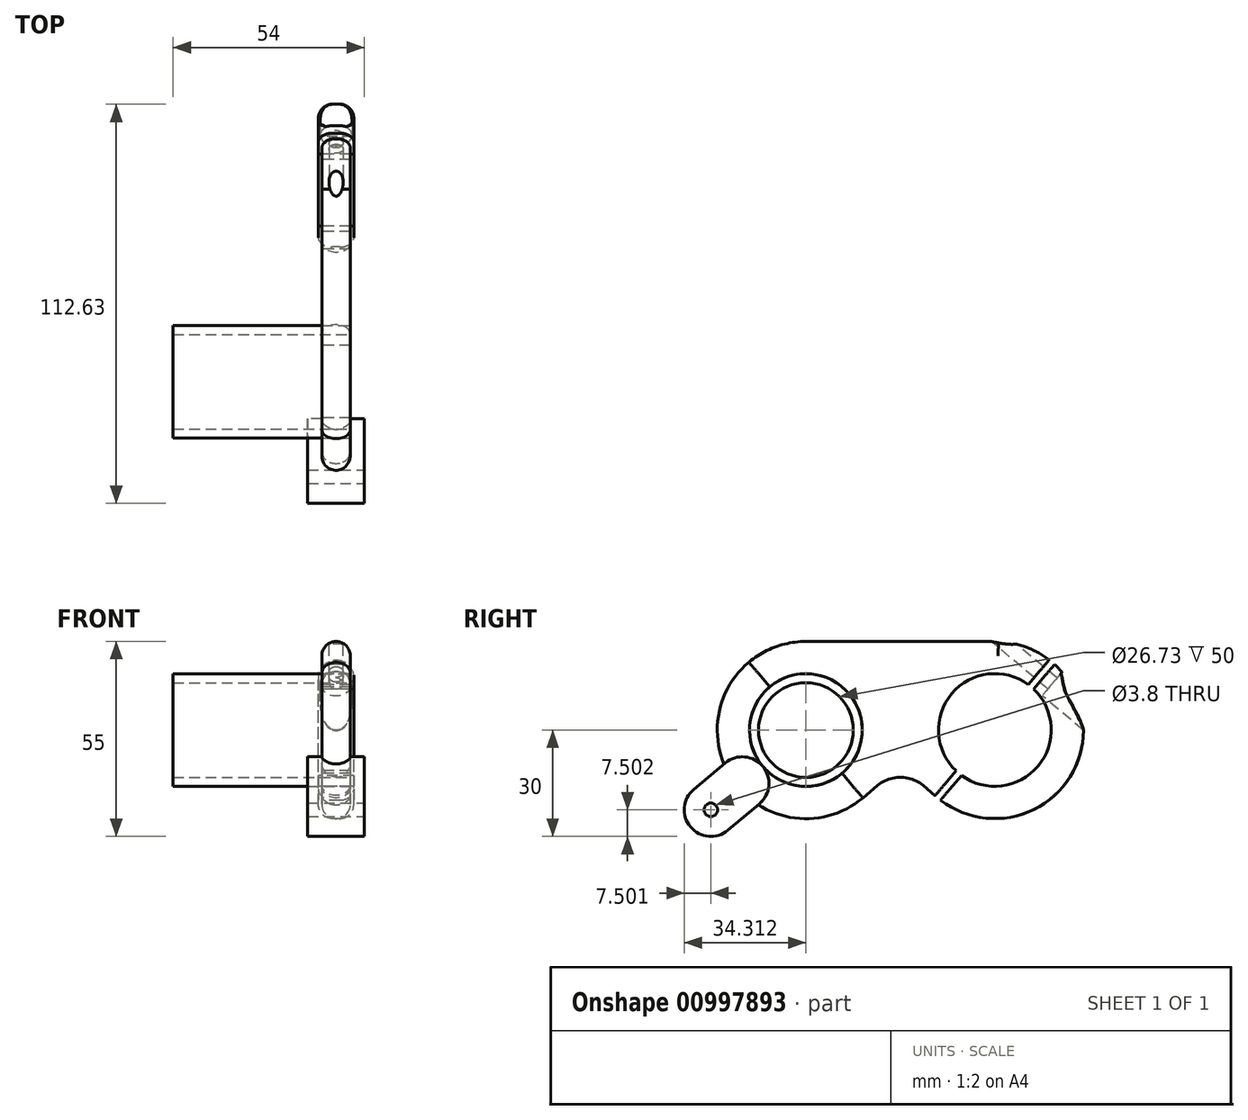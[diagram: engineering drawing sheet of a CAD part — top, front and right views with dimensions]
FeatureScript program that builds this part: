
annotation { "Feature Type Name" : "Feature", "Feature Type Description" : "" }
export const myFeature = defineFeature(function(context is Context, id is Id, definition is map)
    precondition{}
    {
        {
            var Q0;
            Q0=qCreatedBy(makeId("Right.planeOp"),FACE);
            var sketch = newSketch(context, id + "F0", { "sketchPlane" : qUnion([Q0])});
            skCircle(sketch, "E0", {"center": v(0, 0) * mm, "radius": 15.9 * mm});
            skLineSegment(sketch, "E1", {"start": v(-70.5, -0.02) * mm, "end": v(-53.32, -0.02) * mm, "construction": true});
            skCircle(sketch, "E2", {"center": v(-53.32, -0.02) * mm, "radius": 25 * mm});
            skLineSegment(sketch, "E3", {"start": v(-53.32, -0.02) * mm, "end": v(-53.32, 24.98) * mm, "construction": true});
            skLineSegment(sketch, "E4", {"start": v(-53.32, -0.02) * mm, "end": v(-53.32, -25.02) * mm, "construction": true});
            skCircle(sketch, "E5", {"center": v(-80.13, -22.52) * mm, "radius": 7.5 * mm});
            skLineSegment(sketch, "E6", {"start": v(-53.32, -0.02) * mm, "end": v(-80.13, -22.52) * mm, "construction": true});
            skCircle(sketch, "E7", {"center": v(-80.13, -22.52) * mm, "radius": 1.9 * mm});
            skLineSegment(sketch, "E8", {"start": v(-80.13, -22.52) * mm, "end": v(-75.3, -28.26) * mm, "construction": true});
            skLineSegment(sketch, "E9", {"start": v(-80.13, -22.52) * mm, "end": v(-84.95, -16.77) * mm, "construction": true});
            skCircle(sketch, "E10", {"center": v(-53.32, -0.02) * mm, "radius": 15.9 * mm});
            skLineSegment(sketch, "E11", {"start": v(0, 0) * mm, "end": v(0, 15.9) * mm, "construction": true});
            skLineSegment(sketch, "E12", {"start": v(0, 0) * mm, "end": v(0, -15.9) * mm, "construction": true});
            skLineSegment(sketch, "E13", {"start": v(1, 15.87) * mm, "end": v(1, 24.98) * mm});
            skCircle(sketch, "E14.converted", {"center": v(0, 0) * mm, "radius": 25 * mm});
            skLineSegment(sketch, "E15", {"start": v(1, 24.98) * mm, "end": v(-53.32, 24.98) * mm});
            skLineSegment(sketch, "E16", {"start": v(-53.32, -0.02) * mm, "end": v(-69.39, 19.13) * mm});
            skLineSegment(sketch, "E17", {"start": v(-53.32, -0.02) * mm, "end": v(-37.25, -19.17) * mm});
            skLineSegment(sketch, "E18", {"start": v(-37.25, -19.17) * mm, "end": v(-26.65, -10.28) * mm});
            skLineSegment(sketch, "E19", {"start": v(16.07, 19.15) * mm, "end": v(-16.07, -19.15) * mm, "construction": true});
            skLineSegment(sketch, "E20", {"start": v(-16.07, -19.15) * mm, "end": v(-26.65, -10.28) * mm});
            skLineSegment(sketch, "E21", {"start": v(16.82, 18.5) * mm, "end": v(-15.3, -19.78) * mm});
            skLineSegment(sketch, "E22", {"start": v(19.58, 15.55) * mm, "end": v(14.95, 10.03) * mm});
            skLineSegment(sketch, "E23", {"start": v(14.95, 10.03) * mm, "end": v(24.95, 1.65) * mm});
            skLineSegment(sketch, "E24", {"start": v(15.3, 19.78) * mm, "end": v(-16.84, -18.5) * mm});
            skLineSegment(sketch, "E25", {"start": v(-11.91, -21.98) * mm, "end": v(-7.51, -16.73) * mm});
            skLineSegment(sketch, "E26", {"start": v(-7.51, -16.73) * mm, "end": v(2.23, -24.9) * mm});
            skPoint(sketch, "E27", {"position": v(13.18, 15.7) * mm});
            skLineSegment(sketch, "E28", {"start": v(13.18, 15.7) * mm, "end": v(10.9, 17.62) * mm, "construction": true});
            skLineSegment(sketch, "E29", {"start": v(-84.95, -16.77) * mm, "end": v(-73.88, -7.48) * mm});
            skLineSegment(sketch, "E30", {"start": v(-75.3, -28.26) * mm, "end": v(-64.24, -18.97) * mm});
            skLineSegment(sketch, "E31", {"start": v(-73.88, -7.48) * mm, "end": v(-68.88, -3.29) * mm});
            skLineSegment(sketch, "E32", {"start": v(-59.38, -14.72) * mm, "end": v(-64.24, -18.97) * mm});
            skSolve(sketch);
        }
        {
            var Q0;
            {var subQ4=sQuery(id+"F0.wireOp",EDGE,"4b9Ultii-NDLb-Hdy1-wgni-m4wKdF3KNtY6");Q0=makeQuery(id+"F0.imprint","IMPRINT",FACE,{"disambiguationData":[TD([[makeQuery(id+"F0.imprint","IMPRINT",EDGE,{"derivedFrom":subQ4}),1.0]])]});}
            var Q1;
            {var subQ6=sQuery(id+"F0.wireOp",EDGE,"Wf0zkuJS-PnXJ-hlOs-DL1g-wqgcpQEXs6ay");var subQ7=sQuery(id+"F0.wireOp",EDGE,"r5HR3Vc3-aV66-gJRk-fCIw-dcTSZV9Szoix");var subQ8=makeQuery(id+"F0.imprint","INTERSECT",VERTEX,{"derivedFrom":[subQ7,subQ6]});Q1=makeQuery(id+"F0.imprint","IMPRINT",FACE,{"disambiguationData":[TD([[makeQuery(id+"F0.imprint","IMPRINT",EDGE,{"disambiguationData":[TD([[subQ8,1.0]])],"derivedFrom":subQ7}),-1.0]])]});}
            var Q2;
            {var subQ4=sQuery(id+"F0.wireOp",EDGE,"J3v9ANAV-t0TG-syF7-68v8-S9FZO05cP5r5");Q2=makeQuery(id+"F0.imprint","IMPRINT",FACE,{"disambiguationData":[TD([[makeQuery(id+"F0.imprint","IMPRINT",EDGE,{"derivedFrom":subQ4}),-1.0]])]});}
            var Q3;
            {var subQ0=sQuery(id+"F0.wireOp",EDGE,"hCOq8FCj-mZPl-xb8t-M9cf-22ctuRcThsnU");Q3=makeQuery(id+"F0.imprint","IMPRINT",FACE,{"disambiguationData":[TD([[makeQuery(id+"F0.imprint","IMPRINT",EDGE,{"derivedFrom":subQ0}),-1.0]])]});}
            var Q4;
            Q4=makeQuery(id+"F0.imprint","IMPRINT",FACE,{"disambiguationData":[TD([[makeQuery(id+"F0.imprint","IMPRINT",EDGE,{"derivedFrom":sQuery(id+"F0.wireOp",EDGE,"5sShV3aE-jCGE-nKPt-bFNu-OAMkQITm1cGi")}),-1.0]])]});
            var Q5;
            {var subQ1=sQuery(id+"F0.wireOp",EDGE,"E0");var subQ3=sQuery(id+"F0.wireOp",EDGE,"c6EyPIpG-ZPuY-48oV-pUW5-DYLZiXgc12xN");var subQ4=makeQuery(id+"F0.imprint","INTERSECT",VERTEX,{"derivedFrom":[subQ1,subQ3]});Q5=makeQuery(id+"F0.imprint","IMPRINT",FACE,{"disambiguationData":[TD([[makeQuery(id+"F0.imprint","IMPRINT",EDGE,{"disambiguationData":[TD([[subQ4,-1.0]])],"derivedFrom":subQ3}),1.0]])]});}
            var Q6;
            {var subQ0=sQuery(id+"F0.wireOp",EDGE,"E13");Q6=makeQuery(id+"F0.imprint","IMPRINT",FACE,{"disambiguationData":[TD([[makeQuery(id+"F0.imprint","IMPRINT",EDGE,{"derivedFrom":subQ0}),1.0]])]});}
            var Q7;
            {var subQ0=sQuery(id+"F0.wireOp",EDGE,"YhiGqcQh-Guml-Ccj6-1uuS-Ju1MmWkPXmzD");Q7=makeQuery(id+"F0.imprint","IMPRINT",FACE,{"disambiguationData":[TD([[makeQuery(id+"F0.imprint","IMPRINT",EDGE,{"derivedFrom":subQ0}),1.0]])]});}
            var Q8;
            {var subQ0=sQuery(id+"F0.wireOp",EDGE,"R5sLn8GK-Xx1C-SiDK-5Llo-cecynse5X5UR");Q8=makeQuery(id+"F0.imprint","IMPRINT",FACE,{"disambiguationData":[TD([[makeQuery(id+"F0.imprint","IMPRINT",EDGE,{"derivedFrom":subQ0}),1.0]])]});}
            var Q9;
            {var subQ0=sQuery(id+"F0.wireOp",EDGE,"flGuJ2Ts-OsDQ-HMHF-BLlG-PwGXolJ0vegO");Q9=makeQuery(id+"F0.imprint","IMPRINT",FACE,{"disambiguationData":[TD([[makeQuery(id+"F0.imprint","IMPRINT",EDGE,{"derivedFrom":subQ0}),-1.0]])]});}
            var Q10;
            {var subQ1=sQuery(id+"F0.wireOp",EDGE,"E15");Q10=makeQuery(id+"F0.imprint","IMPRINT",FACE,{"disambiguationData":[TD([[makeQuery(id+"F0.imprint","IMPRINT",EDGE,{"derivedFrom":subQ1}),1.0]])]});}
            var Q11;
            {var subQ0=sQuery(id+"F0.wireOp",EDGE,"E13");Q11=makeQuery(id+"F0.imprint","IMPRINT",FACE,{"disambiguationData":[TD([[makeQuery(id+"F0.imprint","IMPRINT",EDGE,{"derivedFrom":subQ0}),-1.0]])]});}
            var Q12;
            {var subQ0=sQuery(id+"F0.wireOp",EDGE,"E18");Q12=makeQuery(id+"F0.imprint","IMPRINT",FACE,{"disambiguationData":[TD([[makeQuery(id+"F0.imprint","IMPRINT",EDGE,{"derivedFrom":subQ0}),1.0]])]});}
            var Q13;
            {var subQ1=sQuery(id+"F0.wireOp",EDGE,"E2");var subQ7=makeQuery(id+"F0.imprint","INTERSECT",VERTEX,{"derivedFrom":[subQ1,sQuery(id+"F0.wireOp",EDGE,"E15")]});Q13=makeQuery(id+"F0.imprint","IMPRINT",FACE,{"disambiguationData":[TD([[makeQuery(id+"F0.imprint","IMPRINT",EDGE,{"disambiguationData":[TD([[subQ7,-1.0]])],"derivedFrom":subQ1}),1.0]])]});}
            extrude(context, id + "F1", {"entities" : qUnion([Q0, Q1, Q2, Q3, Q4, Q5, Q6, Q7, Q8, Q9, Q10, Q11, Q12, Q13]), "endBound" : BoundingType.SYMMETRIC, "depth" : 8 * mm, "offsetDistance" : 25 * mm});
        }
        {
            var Q0;
            {var subQ0=sQuery(id+"F0.wireOp",EDGE,"E16");var subQ3=sQuery(id+"F0.wireOp",EDGE,"E10");var subQ4=makeQuery(id+"F0.imprint","INTERSECT",VERTEX,{"derivedFrom":[subQ3,subQ0]});Q0=makeQuery(id+"F0.imprint","IMPRINT",FACE,{"disambiguationData":[TD([[makeQuery(id+"F0.imprint","IMPRINT",EDGE,{"disambiguationData":[TD([[subQ4,-1.0]])],"derivedFrom":subQ3}),-1.0]])]});}
            var Q1;
            {var subQ0=sQuery(id+"F0.wireOp",EDGE,"E29");var subQ1=sQuery(id+"F0.wireOp",EDGE,"E2");var subQ2=makeQuery(id+"F0.imprint","INTERSECT",VERTEX,{"derivedFrom":[subQ1,subQ0]});Q1=makeQuery(id+"F0.imprint","IMPRINT",FACE,{"disambiguationData":[TD([[makeQuery(id+"F0.imprint","IMPRINT",EDGE,{"disambiguationData":[TD([[subQ2,-1.0]])],"derivedFrom":subQ1}),1.0]])]});}
            var Q2;
            {var subQ0=sQuery(id+"F0.wireOp",EDGE,"bRgBHCgO-Ik4q-WNOr-8PJ1-55WgfLpFXWza");var subQ3=sQuery(id+"F0.wireOp",EDGE,"E29");var subQ5=makeQuery(id+"F0.imprint","INTERSECT",VERTEX,{"derivedFrom":[subQ0,subQ3]});Q2=makeQuery(id+"F0.imprint","IMPRINT",FACE,{"disambiguationData":[TD([[makeQuery(id+"F0.imprint","IMPRINT",EDGE,{"disambiguationData":[TD([[subQ5,1.0]])],"derivedFrom":subQ3}),1.0]])]});}
            var Q3;
            {var subQ0=sQuery(id+"F0.wireOp",EDGE,"bRgBHCgO-Ik4q-WNOr-8PJ1-55WgfLpFXWza");var subQ3=sQuery(id+"F0.wireOp",EDGE,"E30");var subQ5=makeQuery(id+"F0.imprint","INTERSECT",VERTEX,{"derivedFrom":[subQ0,subQ3]});Q3=makeQuery(id+"F0.imprint","IMPRINT",FACE,{"disambiguationData":[TD([[makeQuery(id+"F0.imprint","IMPRINT",EDGE,{"disambiguationData":[TD([[subQ5,1.0]])],"derivedFrom":subQ3}),-1.0]])]});}
            var Q4;
            {var subQ0=sQuery(id+"F0.wireOp",EDGE,"E31");Q4=makeQuery(id+"F0.imprint","IMPRINT",FACE,{"disambiguationData":[TD([[makeQuery(id+"F0.imprint","IMPRINT",EDGE,{"derivedFrom":subQ0}),-1.0]])]});}
            extrude(context, id + "F2", {"entities" : qUnion([Q0, Q1, Q2, Q3, Q4]), "endBound" : BoundingType.SYMMETRIC, "depth" : 8 * mm, "offsetDistance" : 25 * mm});
        }
        {
            var Q0;
            Q0=makeQuery(id+"F1.opExtrude","SWEPT_EDGE",EDGE,{"disambiguationData":[OSD([sQuery(id+"F0.wireOp",EDGE,"E18"),sQuery(id+"F0.wireOp",EDGE,"E20")])]});
            fillet(context, id + "F3", {"entities" : qUnion([Q0]), "tangentPropagation" : true, "radius" : 10 * mm, "defaultsChanged" : true, "vertexSettings" : [], "allowEdgeOverflow" : false});
        }
        {
            var Q0;
            Q0=makeQuery(id+"F1.opExtrude","CAP_EDGE",EDGE,{"disambiguationData":[OSD([sQuery(id+"F0.wireOp",EDGE,"E14.converted")])],"isStart":false});
            var Q1;
            Q1=makeQuery(id+"F1.opExtrude","CAP_EDGE",EDGE,{"disambiguationData":[OSD([sQuery(id+"F0.wireOp",EDGE,"E14.converted")])],"isStart":true});
            var Q2;
            {var subQ0=sQuery(id+"F0.wireOp",EDGE,"E20");var subQ1=sQuery(id+"F0.wireOp",EDGE,"E18");Q2=makeQuery(id+"F3.opFillet","BLEND_EDGE",EDGE,{"blendedFrom":[makeQuery(id+"F1.opExtrude","SWEPT_EDGE",EDGE,{"disambiguationData":[OSD([subQ1,subQ0])]}),makeQuery(id+"F1.opExtrude","CAP_FACE",FACE,{"disambiguationData":[OSD([sQuery(id+"F0.wireOp",EDGE,"E0"),sQuery(id+"F0.wireOp",EDGE,"E2"),sQuery(id+"F0.wireOp",EDGE,"E10"),sQuery(id+"F0.wireOp",EDGE,"E14.converted"),sQuery(id+"F0.wireOp",EDGE,"E15"),sQuery(id+"F0.wireOp",EDGE,"E16"),sQuery(id+"F0.wireOp",EDGE,"E17"),subQ1,sQuery(id+"F0.wireOp",EDGE,"E19"),subQ0])],"isStart":true})],"blendedInto":[makeQuery(id+"F1.opExtrude","CAP_FACE",FACE,{"disambiguationData":[OSD([sQuery(id+"F0.wireOp",EDGE,"E0"),sQuery(id+"F0.wireOp",EDGE,"E2"),sQuery(id+"F0.wireOp",EDGE,"E10"),sQuery(id+"F0.wireOp",EDGE,"E14.converted"),sQuery(id+"F0.wireOp",EDGE,"E15"),sQuery(id+"F0.wireOp",EDGE,"E16"),sQuery(id+"F0.wireOp",EDGE,"E17"),subQ1,sQuery(id+"F0.wireOp",EDGE,"E19"),subQ0])],"isStart":true})]});}
            var Q3;
            {var subQ0=sQuery(id+"F0.wireOp",EDGE,"E20");var subQ1=sQuery(id+"F0.wireOp",EDGE,"E18");Q3=makeQuery(id+"F3.opFillet","BLEND_EDGE",EDGE,{"blendedFrom":[makeQuery(id+"F1.opExtrude","SWEPT_EDGE",EDGE,{"disambiguationData":[OSD([subQ1,subQ0])]}),makeQuery(id+"F1.opExtrude","CAP_FACE",FACE,{"disambiguationData":[OSD([sQuery(id+"F0.wireOp",EDGE,"E0"),sQuery(id+"F0.wireOp",EDGE,"E2"),sQuery(id+"F0.wireOp",EDGE,"E10"),sQuery(id+"F0.wireOp",EDGE,"E14.converted"),sQuery(id+"F0.wireOp",EDGE,"E15"),sQuery(id+"F0.wireOp",EDGE,"E16"),sQuery(id+"F0.wireOp",EDGE,"E17"),subQ1,sQuery(id+"F0.wireOp",EDGE,"E19"),subQ0])],"isStart":false})],"blendedInto":[makeQuery(id+"F1.opExtrude","CAP_FACE",FACE,{"disambiguationData":[OSD([sQuery(id+"F0.wireOp",EDGE,"E0"),sQuery(id+"F0.wireOp",EDGE,"E2"),sQuery(id+"F0.wireOp",EDGE,"E10"),sQuery(id+"F0.wireOp",EDGE,"E14.converted"),sQuery(id+"F0.wireOp",EDGE,"E15"),sQuery(id+"F0.wireOp",EDGE,"E16"),sQuery(id+"F0.wireOp",EDGE,"E17"),subQ1,sQuery(id+"F0.wireOp",EDGE,"E19"),subQ0])],"isStart":false})]});}
            var Q4;
            Q4=makeQuery(id+"F1.opExtrude","CAP_EDGE",EDGE,{"disambiguationData":[OSD([sQuery(id+"F0.wireOp",EDGE,"E2")])],"isStart":true});
            var Q5;
            Q5=makeQuery(id+"F1.opExtrude","CAP_EDGE",EDGE,{"disambiguationData":[OSD([sQuery(id+"F0.wireOp",EDGE,"E2")])],"isStart":false});
            var Q6;
            Q6=makeQuery(id+"F1.opExtrude","CAP_EDGE",EDGE,{"disambiguationData":[OSD([sQuery(id+"F0.wireOp",EDGE,"E15")])],"isStart":false});
            fillet(context, id + "F4", {"entities" : qUnion([Q0, Q1, Q2, Q3, Q4, Q5, Q6]), "tangentPropagation" : true, "radius" : 4 * mm, "defaultsChanged" : true, "vertexSettings" : [], "allowEdgeOverflow" : false});
        }
        {
            var Q0;
            {var subQ0=sQuery(id+"F0.wireOp",EDGE,"E2");Q0=makeQuery(id+"F2.opExtrude","CAP_EDGE",EDGE,{"disambiguationData":[OSD([subQ0]),TDD([makeQuery(id+"F0.imprint","IMPRINT",EDGE,{"disambiguationData":[TD([[makeQuery(id+"F0.imprint","INTERSECT",VERTEX,{"derivedFrom":[subQ0,sQuery(id+"F0.wireOp",EDGE,"iORE6lGe-D1Q3-abtE-zUM2-a5tct9FX5gMR")]}),1.0]])],"derivedFrom":subQ0})])],"isStart":false});}
            var Q1;
            {var subQ0=sQuery(id+"F0.wireOp",EDGE,"E2");Q1=makeQuery(id+"F2.opExtrude","CAP_EDGE",EDGE,{"disambiguationData":[OSD([subQ0]),TDD([makeQuery(id+"F0.imprint","IMPRINT",EDGE,{"disambiguationData":[TD([[makeQuery(id+"F0.imprint","INTERSECT",VERTEX,{"derivedFrom":[subQ0,sQuery(id+"F0.wireOp",EDGE,"iORE6lGe-D1Q3-abtE-zUM2-a5tct9FX5gMR")]}),1.0]])],"derivedFrom":subQ0})])],"isStart":true});}
            var Q2;
            {var subQ0=sQuery(id+"F0.wireOp",EDGE,"E2");Q2=makeQuery(id+"F2.opExtrude","CAP_EDGE",EDGE,{"disambiguationData":[OSD([subQ0]),TDD([makeQuery(id+"F0.imprint","IMPRINT",EDGE,{"disambiguationData":[TD([[makeQuery(id+"F0.imprint","INTERSECT",VERTEX,{"derivedFrom":[subQ0,sQuery(id+"F0.wireOp",EDGE,"E16")]}),-1.0]])],"derivedFrom":subQ0})])],"isStart":true});}
            var Q3;
            {var subQ0=sQuery(id+"F0.wireOp",EDGE,"E2");Q3=makeQuery(id+"F2.opExtrude","CAP_EDGE",EDGE,{"disambiguationData":[OSD([subQ0]),TDD([makeQuery(id+"F0.imprint","IMPRINT",EDGE,{"disambiguationData":[TD([[makeQuery(id+"F0.imprint","INTERSECT",VERTEX,{"derivedFrom":[subQ0,sQuery(id+"F0.wireOp",EDGE,"E17"),sQuery(id+"F0.wireOp",EDGE,"E18")]}),1.0]])],"derivedFrom":subQ0})])],"isStart":true});}
            var Q4;
            {var subQ0=sQuery(id+"F0.wireOp",EDGE,"E2");Q4=makeQuery(id+"F2.opExtrude","CAP_EDGE",EDGE,{"disambiguationData":[OSD([subQ0]),TDD([makeQuery(id+"F0.imprint","IMPRINT",EDGE,{"disambiguationData":[TD([[makeQuery(id+"F0.imprint","INTERSECT",VERTEX,{"derivedFrom":[subQ0,sQuery(id+"F0.wireOp",EDGE,"E16")]}),-1.0]])],"derivedFrom":subQ0})])],"isStart":false});}
            var Q5;
            {var subQ0=sQuery(id+"F0.wireOp",EDGE,"E2");Q5=makeQuery(id+"F2.opExtrude","CAP_EDGE",EDGE,{"disambiguationData":[OSD([subQ0]),TDD([makeQuery(id+"F0.imprint","IMPRINT",EDGE,{"disambiguationData":[TD([[makeQuery(id+"F0.imprint","INTERSECT",VERTEX,{"derivedFrom":[subQ0,sQuery(id+"F0.wireOp",EDGE,"E17"),sQuery(id+"F0.wireOp",EDGE,"E18")]}),1.0]])],"derivedFrom":subQ0})])],"isStart":false});}
            fillet(context, id + "F5", {"entities" : qUnion([Q0, Q1, Q2, Q3, Q4, Q5]), "tangentPropagation" : true, "radius" : 4 * mm, "defaultsChanged" : true, "vertexSettings" : [], "allowEdgeOverflow" : false});
        }
        {
            var Q0;
            {var subQ10=sQuery(id+"F0.wireOp",EDGE,"E22");Q0=makeQuery(id+"F0.imprint","IMPRINT",FACE,{"disambiguationData":[TD([[makeQuery(id+"F0.imprint","IMPRINT",EDGE,{"derivedFrom":subQ10}),-1.0]])]});}
            var Q1;
            {var subQ0=sQuery(id+"F0.wireOp",EDGE,"E25");Q1=makeQuery(id+"F0.imprint","IMPRINT",FACE,{"disambiguationData":[TD([[makeQuery(id+"F0.imprint","IMPRINT",EDGE,{"derivedFrom":subQ0}),-1.0]])]});}
            var Q2;
            {var subQ0=sQuery(id+"F0.wireOp",EDGE,"E22");Q2=makeQuery(id+"F0.imprint","IMPRINT",FACE,{"disambiguationData":[TD([[makeQuery(id+"F0.imprint","IMPRINT",EDGE,{"derivedFrom":subQ0}),1.0]])]});}
            extrude(context, id + "F6", {"entities" : qUnion([Q0, Q1, Q2]), "endBound" : BoundingType.SYMMETRIC, "depth" : 10 * mm, "offsetDistance" : 25 * mm});
        }
        {
            var Q0;
            {var subQ0=sQuery(id+"F0.wireOp",EDGE,"E14.converted");Q0=makeQuery(id+"F6.opExtrude","CAP_EDGE",EDGE,{"disambiguationData":[OSD([subQ0]),TDD([makeQuery(id+"F0.imprint","IMPRINT",EDGE,{"disambiguationData":[TD([[makeQuery(id+"F0.imprint","INTERSECT",VERTEX,{"disambiguationData":[OD(0.0)],"derivedFrom":[subQ0,sQuery(id+"F0.wireOp",EDGE,"E21")]}),1.0]])],"derivedFrom":subQ0})])],"isStart":false});}
            var Q1;
            {var subQ0=sQuery(id+"F0.wireOp",EDGE,"E14.converted");Q1=makeQuery(id+"F6.opExtrude","CAP_EDGE",EDGE,{"disambiguationData":[OSD([subQ0]),TDD([makeQuery(id+"F0.imprint","IMPRINT",EDGE,{"disambiguationData":[TD([[makeQuery(id+"F0.imprint","INTERSECT",VERTEX,{"disambiguationData":[OD(0.0)],"derivedFrom":[subQ0,sQuery(id+"F0.wireOp",EDGE,"E21")]}),1.0]])],"derivedFrom":subQ0})])],"isStart":true});}
            var Q2;
            {var subQ0=sQuery(id+"F0.wireOp",EDGE,"E14.converted");Q2=makeQuery(id+"F6.opExtrude","CAP_EDGE",EDGE,{"disambiguationData":[OSD([subQ0]),TDD([makeQuery(id+"F0.imprint","IMPRINT",EDGE,{"disambiguationData":[TD([[makeQuery(id+"F0.imprint","INTERSECT",VERTEX,{"disambiguationData":[OD(1.0)],"derivedFrom":[subQ0,sQuery(id+"F0.wireOp",EDGE,"E21")]}),-1.0]])],"derivedFrom":subQ0})])],"isStart":false});}
            var Q3;
            {var subQ0=sQuery(id+"F0.wireOp",EDGE,"E14.converted");Q3=makeQuery(id+"F6.opExtrude","CAP_EDGE",EDGE,{"disambiguationData":[OSD([subQ0]),TDD([makeQuery(id+"F0.imprint","IMPRINT",EDGE,{"disambiguationData":[TD([[makeQuery(id+"F0.imprint","INTERSECT",VERTEX,{"disambiguationData":[OD(1.0)],"derivedFrom":[subQ0,sQuery(id+"F0.wireOp",EDGE,"E21")]}),-1.0]])],"derivedFrom":subQ0})])],"isStart":true});}
            fillet(context, id + "F7", {"entities" : qUnion([Q0, Q1, Q2, Q3]), "tangentPropagation" : true, "radius" : 4 * mm, "defaultsChanged" : true, "vertexSettings" : [], "allowEdgeOverflow" : false});
        }
        {
            var Q0;
            Q0=sQuery(id+"F0.wireOp",EDGE,"E28");
            var Q1;
            Q1=sQuery(id+"F0.wireOp",VERTEX,"E27");
            cPlane(context, id + "F8", {"entities" : qUnion([Q0, Q1]), "cplaneType" : CPlaneType.LINE_POINT, "offset" : 25 * mm, "width" : 150 * mm, "height" : 150 * mm});
        }
        {
            var Q0;
            Q0=qCreatedBy(id+"F8.planeOp",FACE);
            var sketch = newSketch(context, id + "F9", { "sketchPlane" : qUnion([Q0])});
            skLineSegment(sketch, "E33", {"start": v(0, 0) * mm, "end": v(0, 20.5) * mm, "construction": true});
            skCircle(sketch, "E34", {"center": v(0, 20.5) * mm, "radius": 2 * mm});
            skSolve(sketch);
        }
        {
            var Q0;
            Q0=makeQuery(id+"F9.imprint","IMPRINT",FACE,{"disambiguationData":[TD([[makeQuery(id+"F9.imprint","IMPRINT",EDGE,{"derivedFrom":sQuery(id+"F9.wireOp",EDGE,"E34")}),1.0]])]});
            extrude(context, id + "F10", {"entities" : qUnion([Q0]), "operationType" : NewBodyOperationType.REMOVE, "oppositeDirection" : true, "depth" : 25 * mm, "offsetDistance" : 25 * mm, "hasSecondDirection" : true, "secondDirectionOppositeDirection" : false, "secondDirectionDepth" : 20 * mm});
        }
        {
            var Q0;
            Q0=qCreatedBy(id+"F8.planeOp",FACE);
            cPlane(context, id + "F11", {"entities" : qUnion([Q0]), "cplaneType" : CPlaneType.OFFSET, "offset" : 4 * mm, "oppositeDirection" : true, "width" : 150 * mm, "height" : 150 * mm});
        }
        {
            var Q0;
            Q0=qCreatedBy(id+"F11.planeOp",FACE);
            var sketch = newSketch(context, id + "F12", { "sketchPlane" : qUnion([Q0])});
            skLineSegment(sketch, "E35", {"start": v(0, 0) * mm, "end": v(0, 20.5) * mm, "construction": true});
            skCircle(sketch, "E36", {"center": v(0, 20.5) * mm, "radius": 4.5 * mm});
            skSolve(sketch);
        }
        {
            var Q0;
            Q0=makeQuery(id+"F12.imprint","IMPRINT",FACE,{"disambiguationData":[TD([[makeQuery(id+"F12.imprint","IMPRINT",EDGE,{"derivedFrom":sQuery(id+"F12.wireOp",EDGE,"E36")}),1.0]])]});
            extrude(context, id + "F13", {"entities" : qUnion([Q0]), "operationType" : NewBodyOperationType.REMOVE, "oppositeDirection" : true, "depth" : 25 * mm, "offsetDistance" : 25 * mm});
        }
        {
            var Q0;
            Q0=makeQuery(id+"F13.boolean.opBoolean","INTERSECT",EDGE,{"derivedFrom":[makeQuery(id+"F7.opFillet","BLEND_FACE",FACE,{"disambiguationData":[OSD([sQuery(id+"F0.wireOp",EDGE,"E14.converted")])]}),makeQuery(id+"F13.opExtrude","SWEPT_FACE",FACE,{"disambiguationData":[OSD([sQuery(id+"F12.wireOp",EDGE,"E36")])]})]});
            fillet(context, id + "F14", {"entities" : qUnion([Q0]), "tangentPropagation" : true, "radius" : 0.1 * mm, "defaultsChanged" : true, "vertexSettings" : [], "allowEdgeOverflow" : false});
        }
        {
            var Q0;
            Q0=makeQuery(id+"F0.imprint","IMPRINT",FACE,{"disambiguationData":[TD([[makeQuery(id+"F0.imprint","IMPRINT",EDGE,{"derivedFrom":sQuery(id+"F0.wireOp",EDGE,"E7")}),-1.0]])]});
            var Q1;
            {var subQ4=sQuery(id+"F0.wireOp",EDGE,"E5");var subQ6=sQuery(id+"F0.wireOp",EDGE,"JqzCysWJ-B6yh-OVyd-IpN0-u0ZRcKMygYIl");var subQ7=makeQuery(id+"F0.imprint","INTERSECT",VERTEX,{"derivedFrom":[subQ4,subQ6]});Q1=makeQuery(id+"F0.imprint","IMPRINT",FACE,{"disambiguationData":[TD([[makeQuery(id+"F0.imprint","IMPRINT",EDGE,{"disambiguationData":[TD([[subQ7,-1.0]])],"derivedFrom":subQ4}),-1.0]])]});}
            var Q2;
            {var subQ0=sQuery(id+"F0.wireOp",EDGE,"U1MWm6BQ-JYbI-BddV-zuCo-ws9ELNz8SrcX");var subQ1=sQuery(id+"F0.wireOp",EDGE,"iORE6lGe-D1Q3-abtE-zUM2-a5tct9FX5gMR");var subQ2=makeQuery(id+"F0.imprint","INTERSECT",VERTEX,{"derivedFrom":[subQ1,subQ0]});Q2=makeQuery(id+"F0.imprint","IMPRINT",FACE,{"disambiguationData":[TD([[makeQuery(id+"F0.imprint","IMPRINT",EDGE,{"disambiguationData":[TD([[subQ2,-1.0]])],"derivedFrom":subQ1}),1.0]])]});}
            var Q3;
            {var subQ0=sQuery(id+"F0.wireOp",EDGE,"U1MWm6BQ-JYbI-BddV-zuCo-ws9ELNz8SrcX");var subQ1=sQuery(id+"F0.wireOp",EDGE,"JqzCysWJ-B6yh-OVyd-IpN0-u0ZRcKMygYIl");var subQ2=makeQuery(id+"F0.imprint","INTERSECT",VERTEX,{"derivedFrom":[subQ1,subQ0]});Q3=makeQuery(id+"F0.imprint","IMPRINT",FACE,{"disambiguationData":[TD([[makeQuery(id+"F0.imprint","IMPRINT",EDGE,{"disambiguationData":[TD([[subQ2,-1.0]])],"derivedFrom":subQ1}),-1.0]])]});}
            extrude(context, id + "F15", {"entities" : qUnion([Q0, Q1, Q2, Q3]), "endBound" : BoundingType.SYMMETRIC, "oppositeDirection" : true, "depth" : 16 * mm, "offsetDistance" : 25 * mm, "hasSecondDirection" : true, "secondDirectionOppositeDirection" : false, "secondDirectionDepth" : 5 * mm});
        }
        {
            var Q0;
            {var subQ0=sQuery(id+"F0.wireOp",EDGE,"E31");Q0=makeQuery(id+"F0.imprint","IMPRINT",FACE,{"disambiguationData":[TD([[makeQuery(id+"F0.imprint","IMPRINT",EDGE,{"derivedFrom":subQ0}),-1.0]])]});}
            extrude(context, id + "F16", {"entities" : qUnion([Q0]), "operationType" : NewBodyOperationType.ADD, "endBound" : BoundingType.SYMMETRIC, "oppositeDirection" : true, "depth" : 16 * mm, "offsetDistance" : 25 * mm});
        }
        {
            var Q0;
            Q0=makeQuery(id+"F1.opExtrude","CAP_FACE",FACE,{"disambiguationData":[OSD([sQuery(id+"F0.wireOp",EDGE,"E0"),sQuery(id+"F0.wireOp",EDGE,"E2"),sQuery(id+"F0.wireOp",EDGE,"E10"),sQuery(id+"F0.wireOp",EDGE,"E14.converted"),sQuery(id+"F0.wireOp",EDGE,"E15"),sQuery(id+"F0.wireOp",EDGE,"E16"),sQuery(id+"F0.wireOp",EDGE,"E17"),sQuery(id+"F0.wireOp",EDGE,"E18"),sQuery(id+"F0.wireOp",EDGE,"E20"),sQuery(id+"F0.wireOp",EDGE,"E24")])],"isStart":false});
            var sketch = newSketch(context, id + "F17", { "sketchPlane" : qUnion([Q0])});
            skCircle(sketch, "E37", {"center": v(-53.32, -0.02) * mm, "radius": 15.9 * mm});
            skCircle(sketch, "E38", {"center": v(-53.32, -0.02) * mm, "radius": 13.37 * mm});
            skSolve(sketch);
        }
        {
            var Q0;
            Q0=makeQuery(id+"F17.imprint","IMPRINT",FACE,{"disambiguationData":[TD([[makeQuery(id+"F17.imprint","IMPRINT",EDGE,{"derivedFrom":sQuery(id+"F17.wireOp",EDGE,"E38")}),-1.0]])]});
            extrude(context, id + "F18", {"entities" : qUnion([Q0]), "oppositeDirection" : true, "depth" : 50 * mm, "offsetDistance" : 25 * mm});
        }
        {
            var Q0;
            {var subQ0=sQuery(id+"F0.wireOp",EDGE,"E30");var subQ1=sQuery(id+"F0.wireOp",EDGE,"E29");var subQ2=sQuery(id+"F0.wireOp",EDGE,"E7");var subQ3=sQuery(id+"F0.wireOp",EDGE,"E5");var subQ4=sQuery(id+"F0.wireOp",EDGE,"E2");var subQ5=sQuery(id+"F0.wireOp",EDGE,"E31");var subQ6=sQuery(id+"F0.wireOp",EDGE,"E10");Q0=makeQuery(id+"F16.boolean.opBoolean","SPLIT",EDGE,{"disambiguationData":[TD([makeQuery(id+"F15.opExtrude","CAP_FACE",FACE,{"disambiguationData":[OSD([subQ4,subQ3,subQ2,subQ1,subQ0])],"isStart":true})])],"derivedFrom":makeQuery(id+"F16.opExtrude","SWEPT_EDGE",EDGE,{"disambiguationData":[OSD([subQ6,subQ5])]})});}
            var Q1;
            {var subQ0=sQuery(id+"F0.wireOp",EDGE,"E32");var subQ1=sQuery(id+"F0.wireOp",EDGE,"E30");var subQ2=sQuery(id+"F0.wireOp",EDGE,"E29");var subQ3=sQuery(id+"F0.wireOp",EDGE,"E10");var subQ4=sQuery(id+"F0.wireOp",EDGE,"E2");var subQ5=sQuery(id+"F0.wireOp",EDGE,"E7");var subQ6=sQuery(id+"F0.wireOp",EDGE,"E5");Q1=makeQuery(id+"F16.boolean.opBoolean","SPLIT",EDGE,{"disambiguationData":[TD([makeQuery(id+"F15.opExtrude","CAP_FACE",FACE,{"disambiguationData":[OSD([subQ4,subQ6,subQ5,subQ2,subQ1])],"isStart":true})])],"derivedFrom":makeQuery(id+"F16.opExtrude","SWEPT_EDGE",EDGE,{"disambiguationData":[OSD([subQ3,subQ0])]})});}
            var Q2;
            {var subQ0=sQuery(id+"F0.wireOp",EDGE,"E30");var subQ1=sQuery(id+"F0.wireOp",EDGE,"E29");var subQ2=sQuery(id+"F0.wireOp",EDGE,"E7");var subQ3=sQuery(id+"F0.wireOp",EDGE,"E5");var subQ4=sQuery(id+"F0.wireOp",EDGE,"E2");var subQ5=sQuery(id+"F0.wireOp",EDGE,"E10");var subQ6=sQuery(id+"F0.wireOp",EDGE,"E31");Q2=makeQuery(id+"F16.boolean.opBoolean","SPLIT",EDGE,{"disambiguationData":[TD([makeQuery(id+"F15.opExtrude","CAP_FACE",FACE,{"disambiguationData":[OSD([subQ4,subQ3,subQ2,subQ1,subQ0])],"isStart":false})])],"derivedFrom":makeQuery(id+"F16.opExtrude","SWEPT_EDGE",EDGE,{"disambiguationData":[OSD([subQ5,subQ6])]})});}
            var Q3;
            {var subQ0=sQuery(id+"F0.wireOp",EDGE,"E30");var subQ1=sQuery(id+"F0.wireOp",EDGE,"E29");var subQ2=sQuery(id+"F0.wireOp",EDGE,"E7");var subQ3=sQuery(id+"F0.wireOp",EDGE,"E5");var subQ4=sQuery(id+"F0.wireOp",EDGE,"E2");var subQ5=sQuery(id+"F0.wireOp",EDGE,"E32");var subQ6=sQuery(id+"F0.wireOp",EDGE,"E10");Q3=makeQuery(id+"F16.boolean.opBoolean","SPLIT",EDGE,{"disambiguationData":[TD([makeQuery(id+"F15.opExtrude","CAP_FACE",FACE,{"disambiguationData":[OSD([subQ4,subQ3,subQ2,subQ1,subQ0])],"isStart":false})])],"derivedFrom":makeQuery(id+"F16.opExtrude","SWEPT_EDGE",EDGE,{"disambiguationData":[OSD([subQ6,subQ5])]})});}
            fillet(context, id + "F19", {"entities" : qUnion([Q0, Q1, Q2, Q3]), "tangentPropagation" : true, "radius" : 7.5 * mm, "defaultsChanged" : false, "vertexSettings" : [], "allowEdgeOverflow" : false});
        }
    });
